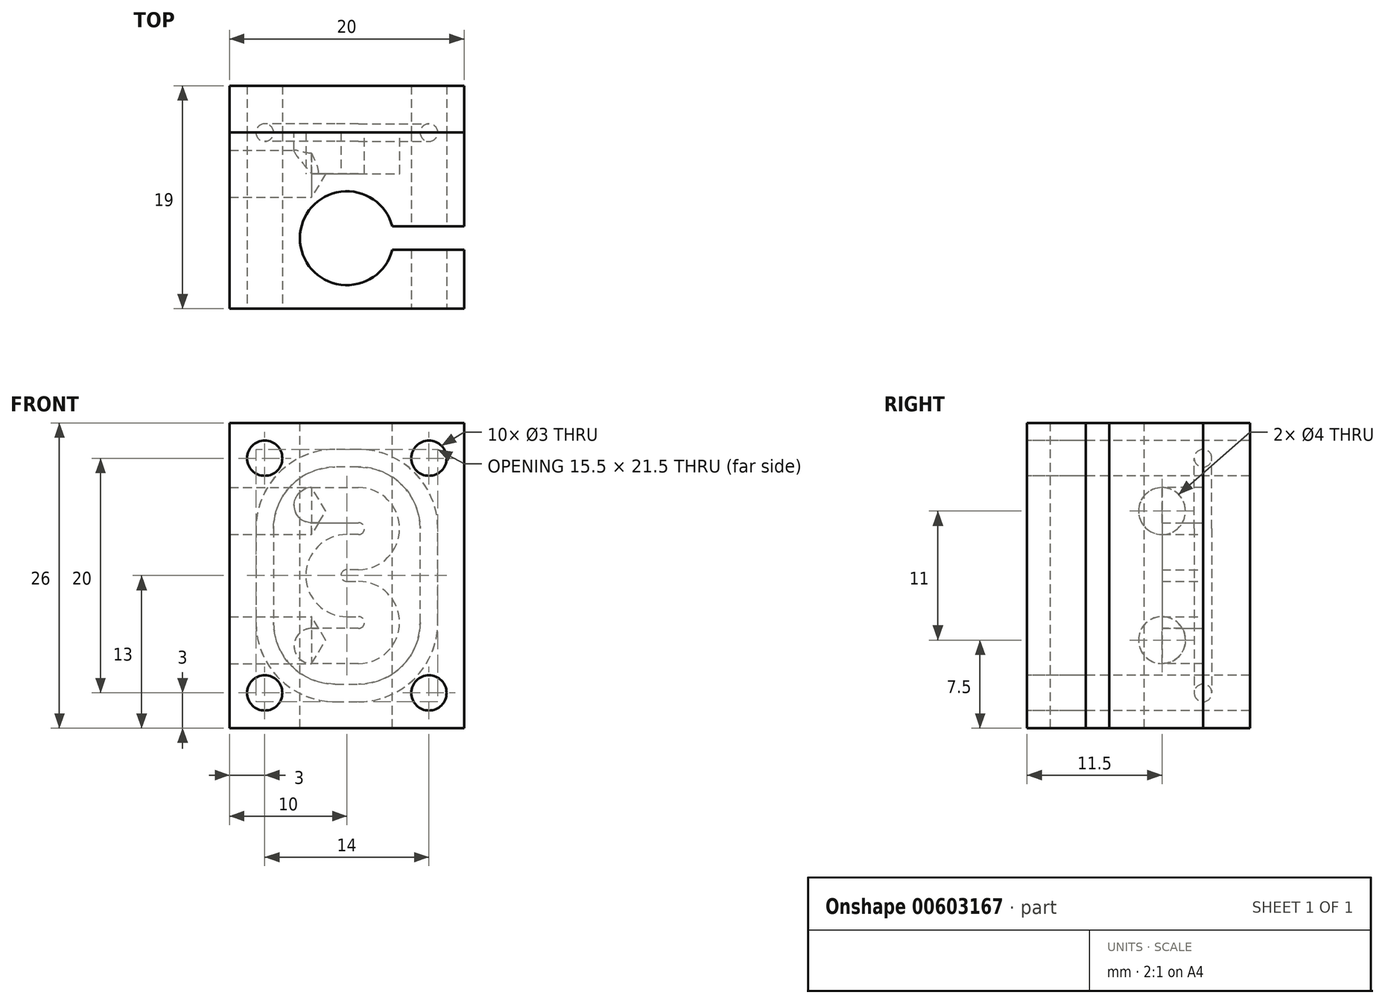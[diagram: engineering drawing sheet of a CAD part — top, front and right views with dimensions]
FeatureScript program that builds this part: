
annotation { "Feature Type Name" : "Feature", "Feature Type Description" : "" }
export const myFeature = defineFeature(function(context is Context, id is Id, definition is map)
    precondition{}
    {
        {
            var Q0;
            Q0=qCreatedBy(makeId("Top.planeOp"),FACE);
            var sketch = newSketch(context, id + "F0", { "sketchPlane" : qUnion([Q0])});
            skLineSegment(sketch, "E0.bottom", {"start": v(-26.95, 5.5) * mm, "end": v(-6.95, 5.5) * mm});
            skLineSegment(sketch, "E0.top", {"start": v(-26.95, 20.5) * mm, "end": v(-6.95, 20.5) * mm});
            skLineSegment(sketch, "E0.left", {"start": v(-26.95, 5.5) * mm, "end": v(-26.95, 20.5) * mm});
            skLineSegment(sketch, "E0.right", {"start": v(-6.95, 5.5) * mm, "end": v(-6.95, 20.5) * mm});
            skCircle(sketch, "E1.0", {"center": v(-16.95, 11.5) * mm, "radius": 4 * mm});
            skLineSegment(sketch, "E2", {"start": v(-13.08, 10.5) * mm, "end": v(-6.95, 10.5) * mm});
            skLineSegment(sketch, "E3", {"start": v(-13.08, 12.5) * mm, "end": v(-6.95, 12.5) * mm});
            skSolve(sketch);
        }
        {
            var Q0;
            {var subQ1=sQuery(id+"F0.wireOp",EDGE,"E0.bottom");Q0=makeQuery(id+"F0.imprint","IMPRINT",FACE,{"disambiguationData":[TD([[makeQuery(id+"F0.imprint","IMPRINT",EDGE,{"derivedFrom":subQ1}),1.0]])]});}
            extrude(context, id + "F1", {"entities" : qUnion([Q0]), "oppositeDirection" : true, "depth" : 26 * mm, "offsetDistance" : 25 * mm});
        }
        {
            var Q0;
            Q0=makeQuery(id+"F1.opExtrude","SWEPT_FACE",FACE,{"disambiguationData":[OSD([sQuery(id+"F0.wireOp",EDGE,"E0.top")])]});
            var sketch = newSketch(context, id + "F2", { "sketchPlane" : qUnion([Q0])});
            skPoint(sketch, "E4", {"position": v(9.95, -23) * mm});
            skPoint(sketch, "E5.0.1.0", {"position": v(9.95, -13) * mm});
            skPoint(sketch, "E5.0.2.0", {"position": v(9.95, -3) * mm});
            skPoint(sketch, "E5.1.0.0", {"position": v(23.95, -23) * mm});
            skPoint(sketch, "E5.1.1.0", {"position": v(23.95, -13) * mm});
            skPoint(sketch, "E5.1.2.0", {"position": v(23.95, -3) * mm});
            skLineSegment(sketch, "E5.direction1", {"start": v(9.95, -23) * mm, "end": v(23.95, -23) * mm, "construction": true});
            skLineSegment(sketch, "E5.direction2", {"start": v(9.95, -23) * mm, "end": v(9.95, -13) * mm, "construction": true});
            skSolve(sketch);
        }
        {
            var Q0;
            Q0=sQuery(id+"F2.wireOp",VERTEX,"E4");
            var Q1;
            Q1=sQuery(id+"F2.wireOp",VERTEX,"E5.0.2.0");
            var Q2;
            Q2=sQuery(id+"F2.wireOp",VERTEX,"E5.1.0.0");
            var Q3;
            Q3=sQuery(id+"F2.wireOp",VERTEX,"E5.1.2.0");
            var Q4;
            Q4=makeQuery(id+"F1.opExtrude","SWEPT_BODY",BODY,{"disambiguationData":[OSD([sQuery(id+"F0.wireOp",EDGE,"E0.bottom"),sQuery(id+"F0.wireOp",EDGE,"E0.top"),sQuery(id+"F0.wireOp",EDGE,"E0.left"),sQuery(id+"F0.wireOp",EDGE,"E0.right"),sQuery(id+"F0.wireOp",EDGE,"E1.0"),sQuery(id+"F0.wireOp",EDGE,"E2"),sQuery(id+"F0.wireOp",EDGE,"E3")])]});
            hole(context, id + "F3", {"style" : HoleStyle.SIMPLE, "endStyle" : HoleEndStyle.THROUGH, "standardTappedOrClearance" : lookupTablePath({ "standard" : "ISO", "size" : "3", "type" : "Drilled" }), "standardBlindInLast" : lookupTablePath({ "standard" : "ISO", "size" : "3", "type" : "Drilled" }), "holeDiameter" : 3 * mm, "majorDiameter" : 5 * mm, "isTappedThrough" : true, "tappedDepth" : 6 * mm, "tapClearance" : 3, "startFromSketch" : true, "locations" : qUnion([Q0, Q1, Q2, Q3]), "scope" : qUnion([Q4])});
        }
        {
            var Q0;
            Q0=makeQuery(id+"F1.opExtrude","SWEPT_FACE",FACE,{"disambiguationData":[OSD([sQuery(id+"F0.wireOp",EDGE,"E0.top")])]});
            var sketch = newSketch(context, id + "F4", { "sketchPlane" : qUnion([Q0])});
            skLineSegment(sketch, "E6", {"start": v(21.45, -19) * mm, "end": v(15.95, -19) * mm});
            skLineSegment(sketch, "E7", {"start": v(13.95, -17) * mm, "end": v(13.95, -17) * mm});
            skLineSegment(sketch, "E8", {"start": v(18.95, -13) * mm, "end": v(18.95, -13) * mm});
            skLineSegment(sketch, "E9", {"start": v(16.95, -11) * mm, "end": v(15.95, -11) * mm});
            skLineSegment(sketch, "E10", {"start": v(13.95, -9) * mm, "end": v(13.95, -9) * mm});
            skLineSegment(sketch, "E11", {"start": v(15.95, -7) * mm, "end": v(21.45, -7) * mm});
            skLineSegment(sketch, "E12", {"start": v(16.95, -15) * mm, "end": v(15.95, -15) * mm});
            skPoint(sketch, "E13.visualSharp", {"position": v(13.95, -19) * mm});
            skArc(sketch, "E13.filletArc", {"start": v(13.95, -17) * mm, "mid": v(14.54, -18.41) * mm, "end": v(15.95, -19) * mm});
            skPoint(sketch, "E14.visualSharp", {"position": v(13.95, -15) * mm});
            skArc(sketch, "E14.filletArc", {"start": v(15.95, -15) * mm, "mid": v(14.54, -15.59) * mm, "end": v(13.95, -17) * mm});
            skPoint(sketch, "E15.visualSharp", {"position": v(18.95, -15) * mm});
            skArc(sketch, "E15.filletArc", {"start": v(16.95, -15) * mm, "mid": v(18.36, -14.41) * mm, "end": v(18.95, -13) * mm});
            skPoint(sketch, "E16.visualSharp", {"position": v(18.95, -11) * mm});
            skArc(sketch, "E16.filletArc", {"start": v(18.95, -13) * mm, "mid": v(18.36, -11.59) * mm, "end": v(16.95, -11) * mm});
            skPoint(sketch, "E17.visualSharp", {"position": v(13.95, -11) * mm});
            skArc(sketch, "E17.filletArc", {"start": v(13.95, -9) * mm, "mid": v(14.54, -10.41) * mm, "end": v(15.95, -11) * mm});
            skPoint(sketch, "E18.visualSharp", {"position": v(13.95, -7) * mm});
            skArc(sketch, "E18.filletArc", {"start": v(15.95, -7) * mm, "mid": v(14.54, -7.59) * mm, "end": v(13.95, -9) * mm});
            skPoint(sketch, "E19", {"position": v(19.45, -19) * mm});
            skPoint(sketch, "E20", {"position": v(19.45, -7) * mm});
            skSolve(sketch);
        }
        {
            var Q0;
            Q0=qCreatedBy(makeId("Right.planeOp"),FACE);
            cPlane(context, id + "F5", {"entities" : qUnion([Q0]), "cplaneType" : CPlaneType.OFFSET, "offset" : 16.95 * mm, "oppositeDirection" : true, "width" : 150 * mm, "height" : 150 * mm});
        }
        {
            var Q0;
            Q0=qCreatedBy(id+"F5.planeOp",FACE);
            var sketch = newSketch(context, id + "F6", { "sketchPlane" : qUnion([Q0])});
            skPoint(sketch, "E21.0", {"position": v(20.5, -7) * mm});
            skLineSegment(sketch, "E22.bottom", {"start": v(17, -8.5) * mm, "end": v(24, -8.5) * mm});
            skLineSegment(sketch, "E22.top", {"start": v(17, -5.5) * mm, "end": v(24, -5.5) * mm});
            skLineSegment(sketch, "E22.left", {"start": v(17, -8.5) * mm, "end": v(17, -5.5) * mm});
            skLineSegment(sketch, "E22.right", {"start": v(24, -8.5) * mm, "end": v(24, -5.5) * mm});
            skSolve(sketch);
        }
        {
            var Q0;
            Q0=makeQuery(id+"F6.imprint","IMPRINT",FACE,{"disambiguationData":[TD([[makeQuery(id+"F6.imprint","IMPRINT",EDGE,{"derivedFrom":sQuery(id+"F6.wireOp",EDGE,"E22.bottom")}),1.0]])]});
            var Q1;
            Q1=sQuery(id+"F4.wireOp",EDGE,"E11");
            var Q2;
            Q2=sQuery(id+"F4.wireOp",EDGE,"E18.filletArc");
            var Q3;
            Q3=sQuery(id+"F4.wireOp",EDGE,"E10");
            var Q4;
            Q4=sQuery(id+"F4.wireOp",EDGE,"E17.filletArc");
            var Q5;
            Q5=sQuery(id+"F4.wireOp",EDGE,"E9");
            var Q6;
            Q6=sQuery(id+"F4.wireOp",EDGE,"E16.filletArc");
            var Q7;
            Q7=sQuery(id+"F4.wireOp",EDGE,"E8");
            var Q8;
            Q8=sQuery(id+"F4.wireOp",EDGE,"E15.filletArc");
            var Q9;
            Q9=sQuery(id+"F4.wireOp",EDGE,"E12");
            var Q10;
            Q10=sQuery(id+"F4.wireOp",EDGE,"E14.filletArc");
            var Q11;
            Q11=sQuery(id+"F4.wireOp",EDGE,"E7");
            var Q12;
            Q12=sQuery(id+"F4.wireOp",EDGE,"E13.filletArc");
            var Q13;
            Q13=sQuery(id+"F4.wireOp",EDGE,"E6");
            sweep(context, id + "F7", {"operationType" : NewBodyOperationType.REMOVE, "profiles" : qUnion([Q0]), "path" : qUnion([Q1, Q2, Q3, Q4, Q5, Q6, Q7, Q8, Q9, Q10, Q11, Q12, Q13])});
        }
        {
            var Q0;
            Q0=makeQuery(id+"F7.boolean.opBoolean","COPY",EDGE,{"derivedFrom":makeQuery(id+"F7.opSweep","CAP_EDGE",EDGE,{"disambiguationData":[OSD([sQuery(id+"F4.wireOp",VERTEX,"E11.end"),sQuery(id+"F6.wireOp",EDGE,"E22.top")])],"isStart":true})});
            var Q1;
            Q1=makeQuery(id+"F7.boolean.opBoolean","COPY",EDGE,{"derivedFrom":makeQuery(id+"F7.opSweep","CAP_EDGE",EDGE,{"disambiguationData":[OSD([sQuery(id+"F4.wireOp",VERTEX,"E11.end"),sQuery(id+"F6.wireOp",EDGE,"E22.bottom")])],"isStart":true})});
            var Q2;
            Q2=makeQuery(id+"F7.boolean.opBoolean","COPY",EDGE,{"derivedFrom":makeQuery(id+"F7.opSweep","CAP_EDGE",EDGE,{"disambiguationData":[OSD([sQuery(id+"F4.wireOp",VERTEX,"E6.start"),sQuery(id+"F6.wireOp",EDGE,"E22.top")])],"isStart":false})});
            var Q3;
            Q3=makeQuery(id+"F7.boolean.opBoolean","COPY",EDGE,{"derivedFrom":makeQuery(id+"F7.opSweep","CAP_EDGE",EDGE,{"disambiguationData":[OSD([sQuery(id+"F4.wireOp",VERTEX,"E6.start"),sQuery(id+"F6.wireOp",EDGE,"E22.bottom")])],"isStart":false})});
            fillet(context, id + "F8", {"entities" : qUnion([Q0, Q1, Q2, Q3]), "radius" : 1.5 * mm, "tangentPropagation" : true, "allowEdgeOverflow" : false});
        }
        {
            var Q0;
            Q0=makeQuery(id+"F1.opExtrude","SWEPT_FACE",FACE,{"disambiguationData":[OSD([sQuery(id+"F0.wireOp",EDGE,"E0.left")])]});
            var sketch = newSketch(context, id + "F9", { "sketchPlane" : qUnion([Q0])});
            skPoint(sketch, "E23", {"position": v(-17, -18.5) * mm});
            skPoint(sketch, "E24", {"position": v(-17, -7.5) * mm});
            skSolve(sketch);
        }
        {
            var Q0;
            Q0=sQuery(id+"F9.wireOp",VERTEX,"E24");
            var Q1;
            Q1=sQuery(id+"F9.wireOp",VERTEX,"E23");
            var Q2;
            Q2=makeQuery(id+"F1.opExtrude","SWEPT_BODY",BODY,{"disambiguationData":[OSD([sQuery(id+"F0.wireOp",EDGE,"E0.bottom"),sQuery(id+"F0.wireOp",EDGE,"E0.top"),sQuery(id+"F0.wireOp",EDGE,"E0.left"),sQuery(id+"F0.wireOp",EDGE,"E0.right"),sQuery(id+"F0.wireOp",EDGE,"E1.0"),sQuery(id+"F0.wireOp",EDGE,"E2"),sQuery(id+"F0.wireOp",EDGE,"E3")])]});
            hole(context, id + "F10", {"style" : HoleStyle.SIMPLE, "endStyle" : HoleEndStyle.BLIND, "holeDiameter" : 4 * mm, "majorDiameter" : 5 * mm, "holeDepth" : 7 * mm, "isTappedThrough" : true, "tappedDepth" : 6 * mm, "tapClearance" : 3, "startFromSketch" : true, "locations" : qUnion([Q0, Q1]), "scope" : qUnion([Q2])});
        }
        {
            var Q0;
            Q0=makeQuery(id+"F1.opExtrude","SWEPT_FACE",FACE,{"disambiguationData":[OSD([sQuery(id+"F0.wireOp",EDGE,"E0.bottom")])]});
            var Q1;
            Q1=makeQuery(id+"F1.opExtrude","SWEPT_FACE",FACE,{"disambiguationData":[OSD([sQuery(id+"F0.wireOp",EDGE,"E0.top")])]});
            var Q2;
            Q2=makeQuery(id+"F1.opExtrude","SWEPT_FACE",FACE,{"disambiguationData":[OSD([sQuery(id+"F0.wireOp",EDGE,"E0.top")])]});
            extrude(context, id + "F11", {"entities" : qUnion([Q0]), "endBound" : BoundingType.UP_TO_SURFACE, "oppositeDirection" : true, "depth" : 25 * mm, "endBoundEntityFace" : qUnion([Q1]), "hasOffset" : true, "offsetDistance" : 4 * mm, "offsetOppositeDirection" : true, "hasSecondDirection" : true, "secondDirectionBound" : BoundingType.UP_TO_SURFACE, "secondDirectionOppositeDirection" : true, "secondDirectionDepth" : 25 * mm, "secondDirectionBoundEntityFace" : qUnion([Q2])});
        }
        {
            var Q0;
            Q0=makeQuery(id+"F1.opExtrude","SWEPT_FACE",FACE,{"disambiguationData":[OSD([sQuery(id+"F0.wireOp",EDGE,"E0.top")])]});
            var sketch = newSketch(context, id + "F12", { "sketchPlane" : qUnion([Q0])});
            skLineSegment(sketch, "E25.bottom", {"start": v(17.95, -23) * mm, "end": v(15.95, -23) * mm});
            skLineSegment(sketch, "E25.top", {"start": v(17.95, -3) * mm, "end": v(15.95, -3) * mm});
            skLineSegment(sketch, "E25.left", {"start": v(23.95, -17) * mm, "end": v(23.95, -9) * mm});
            skLineSegment(sketch, "E25.right", {"start": v(9.95, -17) * mm, "end": v(9.95, -9) * mm});
            skPoint(sketch, "E26.visualSharp", {"position": v(9.95, -23) * mm});
            skArc(sketch, "E26.filletArc", {"start": v(9.95, -17) * mm, "mid": v(11.7, -21.24) * mm, "end": v(15.95, -23) * mm});
            skPoint(sketch, "E27.visualSharp", {"position": v(23.95, -23) * mm});
            skArc(sketch, "E27.filletArc", {"start": v(17.95, -23) * mm, "mid": v(22.2, -21.24) * mm, "end": v(23.95, -17) * mm});
            skPoint(sketch, "E28.visualSharp", {"position": v(23.95, -3) * mm});
            skArc(sketch, "E28.filletArc", {"start": v(23.95, -9) * mm, "mid": v(22.2, -4.76) * mm, "end": v(17.95, -3) * mm});
            skPoint(sketch, "E29.visualSharp", {"position": v(9.95, -3) * mm});
            skArc(sketch, "E29.filletArc", {"start": v(15.95, -3) * mm, "mid": v(11.7, -4.76) * mm, "end": v(9.95, -9) * mm});
            skSolve(sketch);
        }
        {
            var Q0;
            Q0=qCreatedBy(id+"F5.planeOp",FACE);
            var sketch = newSketch(context, id + "F13", { "sketchPlane" : qUnion([Q0])});
            skPoint(sketch, "E30.0", {"position": v(20.5, -23) * mm});
            skCircle(sketch, "E31", {"center": v(20.5, -23) * mm, "radius": 0.75 * mm});
            skSolve(sketch);
        }
        {
            var Q0;
            Q0=makeQuery(id+"F13.imprint","IMPRINT",FACE,{"disambiguationData":[TD([[makeQuery(id+"F13.imprint","IMPRINT",EDGE,{"derivedFrom":sQuery(id+"F13.wireOp",EDGE,"E31")}),1.0]])]});
            var Q1;
            Q1 = qConstructionFilter(qBodyType(qCreatedBy(id + "F12" ,EDGE), BodyType.WIRE), ConstructionObject.NO);
            sweep(context, id + "F14", {"operationType" : NewBodyOperationType.REMOVE, "profiles" : qUnion([Q0]), "path" : qUnion([Q1])});
        }
        {
            var Q0;
            Q0=makeQuery(id+"F13.imprint","IMPRINT",FACE,{"disambiguationData":[TD([[makeQuery(id+"F13.imprint","IMPRINT",EDGE,{"derivedFrom":sQuery(id+"F13.wireOp",EDGE,"E31")}),1.0]])]});
            var Q1;
            Q1=sQuery(id+"F13.wireOp",EDGE,"E31");
            var Q2;
            Q2 = qConstructionFilter(qBodyType(qCreatedBy(id + "F12" ,EDGE), BodyType.WIRE), ConstructionObject.NO);
            sweep(context, id + "F15", {"profiles" : qUnion([Q0]), "surfaceProfiles" : qUnion([Q1]), "path" : qUnion([Q2])});
        }
    });
